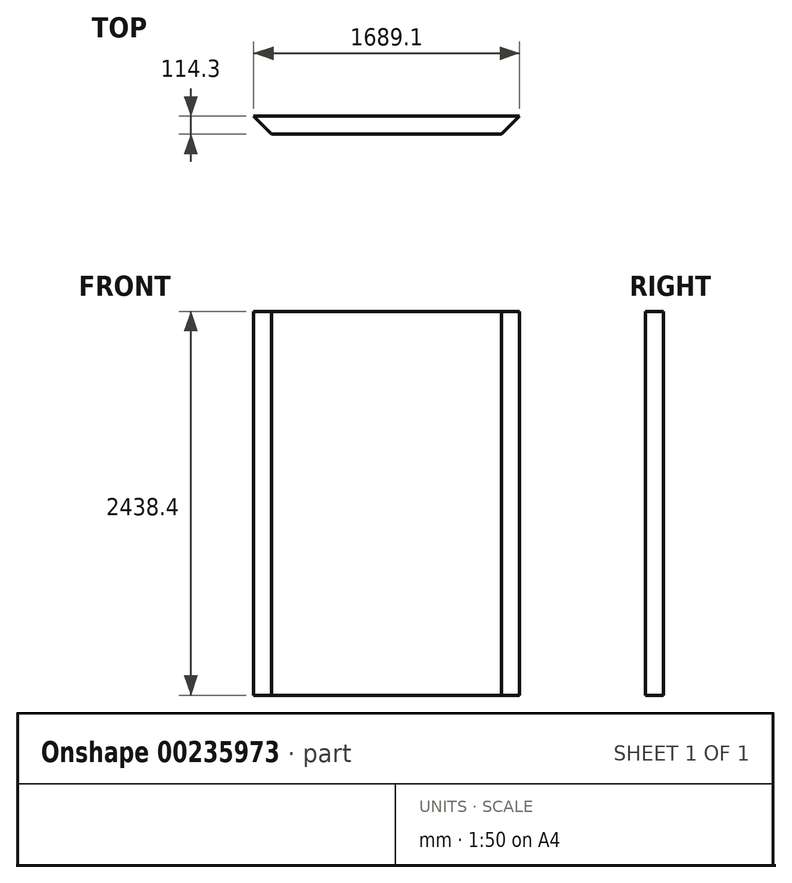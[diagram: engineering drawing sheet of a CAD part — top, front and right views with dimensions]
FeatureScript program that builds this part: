
annotation { "Feature Type Name" : "Feature", "Feature Type Description" : "" }
export const myFeature = defineFeature(function(context is Context, id is Id, definition is map)
    precondition{}
    {
        {
            var Q0;
            Q0=qCreatedBy(makeId("Top.planeOp"),FACE);
            var sketch = newSketch(context, id + "F0", { "sketchPlane" : qUnion([Q0])});
            skLineSegment(sketch, "E0.bottom", {"start": v(730.25, -57.15) * mm, "end": v(-730.25, -57.15) * mm});
            skLineSegment(sketch, "E0.top", {"start": v(730.25, 57.15) * mm, "end": v(-730.25, 57.15) * mm});
            skLineSegment(sketch, "E0.left", {"start": v(730.25, -57.15) * mm, "end": v(730.25, 57.15) * mm});
            skLineSegment(sketch, "E0.right", {"start": v(-730.25, -57.15) * mm, "end": v(-730.25, 57.15) * mm});
            skPoint(sketch, "E0.middle", {"position": v(0, 0) * mm});
            skLineSegment(sketch, "E1", {"start": v(730.25, 57.15) * mm, "end": v(844.55, 57.15) * mm});
            skLineSegment(sketch, "E2", {"start": v(-730.25, 57.15) * mm, "end": v(-844.55, 57.15) * mm});
            skLineSegment(sketch, "E3", {"start": v(-844.55, 57.15) * mm, "end": v(-730.25, -57.15) * mm});
            skLineSegment(sketch, "E4", {"start": v(730.25, -57.15) * mm, "end": v(844.55, 57.15) * mm});
            skSolve(sketch);
        }
        {
            var Q0;
            Q0=makeQuery(id+"F0.imprint","IMPRINT",FACE,{"disambiguationData":[TD([[makeQuery(id+"F0.imprint","IMPRINT",EDGE,{"derivedFrom":sQuery(id+"F0.wireOp",EDGE,"E0.right")}),1.0]])]});
            var Q1;
            Q1=makeQuery(id+"F0.imprint","IMPRINT",FACE,{"disambiguationData":[TD([[makeQuery(id+"F0.imprint","IMPRINT",EDGE,{"derivedFrom":sQuery(id+"F0.wireOp",EDGE,"E0.bottom")}),-1.0]])]});
            var Q2;
            Q2=makeQuery(id+"F0.imprint","IMPRINT",FACE,{"disambiguationData":[TD([[makeQuery(id+"F0.imprint","IMPRINT",EDGE,{"derivedFrom":sQuery(id+"F0.wireOp",EDGE,"E0.left")}),-1.0]])]});
            extrude(context, id + "F1", {"entities" : qUnion([Q0, Q1, Q2]), "depth" : 2438.4 * mm});
        }
    });
